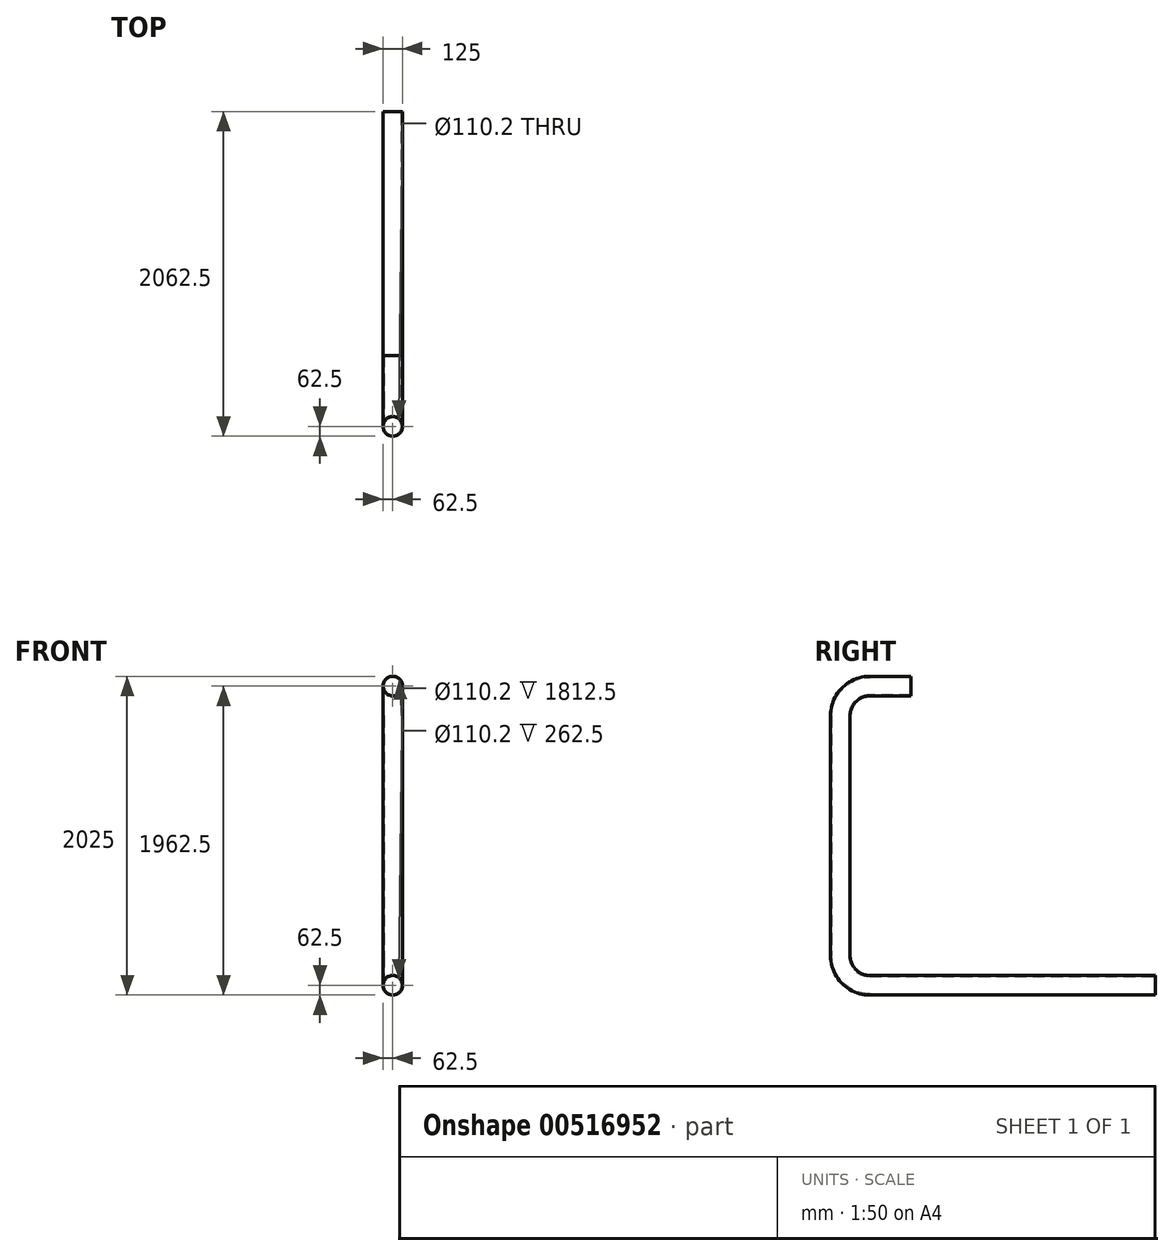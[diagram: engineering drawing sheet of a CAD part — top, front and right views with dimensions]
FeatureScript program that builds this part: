
annotation { "Feature Type Name" : "Feature", "Feature Type Description" : "" }
export const myFeature = defineFeature(function(context is Context, id is Id, definition is map)
    precondition{}
    {
        {
            var Q0;
            Q0=qCreatedBy(makeId("Right.planeOp"),FACE);
            var sketch = newSketch(context, id + "F0", { "sketchPlane" : qUnion([Q0])});
            skLineSegment(sketch, "E0", {"start": v(0, 0) * mm, "end": v(-262.5, 0) * mm});
            skLineSegment(sketch, "E1", {"start": v(-450, -187.5) * mm, "end": v(-450, -1712.5) * mm});
            skPoint(sketch, "E2.visualSharp", {"position": v(-450, 0) * mm});
            skArc(sketch, "E2.filletArc", {"start": v(-262.5, 0) * mm, "mid": v(-395.08, -54.92) * mm, "end": v(-450, -187.5) * mm});
            skLineSegment(sketch, "E3", {"start": v(-262.5, -1900) * mm, "end": v(1550, -1900) * mm});
            skPoint(sketch, "E4.visualSharp", {"position": v(-450, -1900) * mm});
            skArc(sketch, "E4.filletArc", {"start": v(-450, -1712.5) * mm, "mid": v(-395.08, -1845.08) * mm, "end": v(-262.5, -1900) * mm});
            skSolve(sketch);
        }
        {
            var Q0;
            Q0=qCreatedBy(makeId("Front.planeOp"),FACE);
            var sketch = newSketch(context, id + "F1", { "sketchPlane" : qUnion([Q0])});
            skCircle(sketch, "E5", {"center": v(0, 0) * mm, "radius": 62.5 * mm});
            skCircle(sketch, "E6", {"center": v(0, 0) * mm, "radius": 55.1 * mm});
            skSolve(sketch);
        }
        {
            var Q0;
            Q0=makeQuery(id+"F1.imprint","IMPRINT",FACE,{"disambiguationData":[TD([[makeQuery(id+"F1.imprint","IMPRINT",EDGE,{"derivedFrom":sQuery(id+"F1.wireOp",EDGE,"E5")}),1.0]])]});
            var Q1;
            Q1=sQuery(id+"F0.wireOp",EDGE,"E0");
            var Q2;
            Q2=sQuery(id+"F0.wireOp",EDGE,"E2.filletArc");
            var Q3;
            Q3=sQuery(id+"F0.wireOp",EDGE,"E1");
            var Q4;
            Q4=sQuery(id+"F0.wireOp",EDGE,"E4.filletArc");
            var Q5;
            Q5=sQuery(id+"F0.wireOp",EDGE,"E3");
            sweep(context, id + "F2", {"profiles" : qUnion([Q0]), "path" : qUnion([Q1, Q2, Q3, Q4, Q5])});
        }
    });
